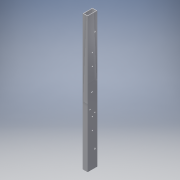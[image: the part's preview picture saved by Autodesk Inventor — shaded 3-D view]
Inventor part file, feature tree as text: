
AUTODESK INVENTOR PART (.ipt)
format: ipt  version: 2016 (Build 200138000, 138)  size: 164,864 bytes
history: native  units: in
note: dims shown in document units (in); Inventor stores cm internally (conversion verified against a paired STEP export)
features: extrude x3, sketch x2
ambient origin geometry x8: Origin, YZ Plane, XZ Plane, XY Plane, X Axis, Y Axis, Z Axis, Center Point
bodies: Solid1 (feature_tree)
feature tree (5):
  extrude  "Extrusion1"  Depth=2.0in
  sketch  "Sketch2"  dims[d2=0.125in d3=28.0in d4=0.0in d6=14.0in d7=1.125in d8=1.0in d9=0.0in d10=0.375in d11=1.5in d14=1.5in d16=10.5in d17=10.5in d18=0.2656in d19=1.0in d20=7.0in d22=9.5in d23=1.0in d25=1.0in d26=7.0in d28=1.0in d29=9.5in d30=0.2656in d31=0.2656in d32=0.5in d33=0.5in d34=1.0in d35=1.5in d36=1.0in d37=0.0in]
  extrude  "Extrusion2"  Depth=28.0in TaperAngle=0.0deg
  extrude  "Extrusion3"  Depth=1.0in
  sketch  "Sketch1"  dims[d0=1.0in d1=2.0in]
